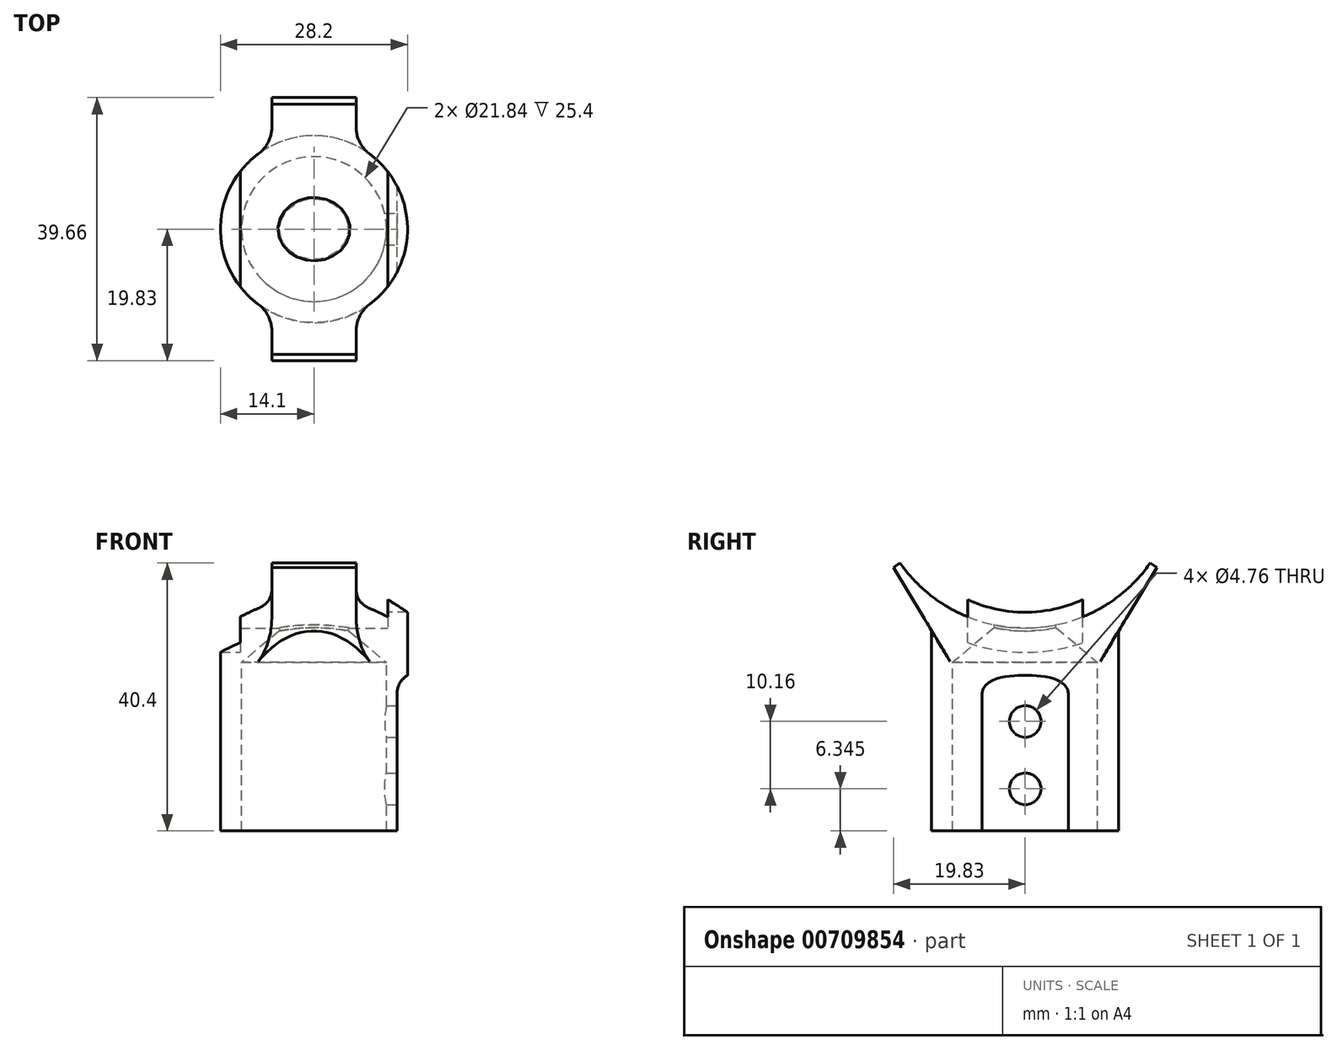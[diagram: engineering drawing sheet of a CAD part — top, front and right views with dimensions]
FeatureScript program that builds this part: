
annotation { "Feature Type Name" : "Feature", "Feature Type Description" : "" }
export const myFeature = defineFeature(function(context is Context, id is Id, definition is map)
    precondition{}
    {
        {
            var Q0;
            Q0=qCreatedBy(makeId("Front.planeOp"),FACE);
            var sketch = newSketch(context, id + "F0", { "sketchPlane" : qUnion([Q0])});
            skLineSegment(sketch, "E0", {"start": v(0, 0) * mm, "end": v(-10.92, -9.16) * mm});
            skLineSegment(sketch, "E1", {"start": v(-10.92, -9.16) * mm, "end": v(-10.92, -34.56) * mm});
            skLineSegment(sketch, "E2", {"start": v(0, 0) * mm, "end": v(0, -71.28) * mm, "construction": true});
            skLineSegment(sketch, "E3", {"start": v(-10.92, -34.56) * mm, "end": v(-14.1, -34.56) * mm});
            skLineSegment(sketch, "E4", {"start": v(-14.1, -34.56) * mm, "end": v(-14.1, 9.52) * mm});
            skLineSegment(sketch, "E5", {"start": v(-14.1, 9.52) * mm, "end": v(0, 9.52) * mm});
            skLineSegment(sketch, "E6", {"start": v(0, 9.52) * mm, "end": v(0, 0) * mm});
            skSolve(sketch);
        }
        {
            var Q0;
            Q0=makeQuery(id+"F0.imprint","IMPRINT",FACE,{"disambiguationData":[TD([[makeQuery(id+"F0.imprint","IMPRINT",EDGE,{"derivedFrom":sQuery(id+"F0.wireOp",EDGE,"E0")}),-1.0]])]});
            var Q1;
            Q1=sQuery(id+"F0.wireOp",EDGE,"E2");
            revolve(context, id + "F1", {"entities" : qUnion([Q0]), "axis" : qUnion([Q1]), "revolveType" : RevolveType.FULL});
        }
        {
            var Q0;
            Q0=makeQuery(id+"F1.opRevolve","SWEPT_EDGE",EDGE,{"disambiguationData":[OSD([sQuery(id+"F0.wireOp",EDGE,"E4"),sQuery(id+"F0.wireOp",EDGE,"E5")])]});
            fillet(context, id + "F2", {"entities" : qUnion([Q0]), "radius" : 2.38 * mm, "tangentPropagation" : true, "allowEdgeOverflow" : false});
        }
        {
            var Q0;
            Q0=qCreatedBy(makeId("Front.planeOp"),FACE);
            var sketch = newSketch(context, id + "F3", { "sketchPlane" : qUnion([Q0])});
            skLineSegment(sketch, "E7", {"start": v(10.92, -10.67) * mm, "end": v(10.92, -36.07) * mm});
            skLineSegment(sketch, "E8", {"start": v(-10.92, -36.07) * mm, "end": v(-10.92, -10.67) * mm});
            skLineSegment(sketch, "E9", {"start": v(-14.1, -36.07) * mm, "end": v(-14.1, 3.17) * mm});
            skLineSegment(sketch, "E10", {"start": v(12.5, -13.84) * mm, "end": v(12.5, -38.6) * mm});
            skLineSegment(sketch, "E11", {"start": v(15.68, -10.67) * mm, "end": v(18.86, -10.67) * mm});
            skLineSegment(sketch, "E12", {"start": v(18.86, -10.67) * mm, "end": v(18.86, -38.6) * mm});
            skLineSegment(sketch, "E13", {"start": v(18.86, -38.6) * mm, "end": v(12.5, -38.6) * mm});
            skPoint(sketch, "E14.visualSharp", {"position": v(12.5, -10.67) * mm});
            skArc(sketch, "E14.filletArc", {"start": v(15.68, -10.67) * mm, "mid": v(13.44, -11.6) * mm, "end": v(12.5, -13.84) * mm});
            skSolve(sketch);
        }
        {
            var Q0;
            Q0=makeQuery(id+"F3.imprint","IMPRINT",FACE,{"disambiguationData":[TD([[makeQuery(id+"F3.imprint","IMPRINT",EDGE,{"derivedFrom":sQuery(id+"F3.wireOp",EDGE,"E10")}),1.0]])]});
            extrude(context, id + "F4", {"entities" : qUnion([Q0]), "operationType" : NewBodyOperationType.REMOVE, "depth" : 25.4 * mm, "hasSecondDirection" : true, "secondDirectionOppositeDirection" : true, "secondDirectionDepth" : 25.4 * mm});
        }
        {
            var Q0;
            Q0=makeQuery(id+"F4.boolean.opBoolean","COPY",FACE,{"derivedFrom":makeQuery(id+"F4.opExtrude","SWEPT_FACE",FACE,{"disambiguationData":[OSD([sQuery(id+"F3.wireOp",EDGE,"E10")])]})});
            var sketch = newSketch(context, id + "F5", { "sketchPlane" : qUnion([Q0])});
            skLineSegment(sketch, "E15", {"start": v(0, -34.56) * mm, "end": v(0, -13.84) * mm, "construction": true});
            skCircle(sketch, "E16", {"center": v(0, -18.05) * mm, "radius": 2.38 * mm});
            skCircle(sketch, "E17", {"center": v(0, -28.21) * mm, "radius": 2.38 * mm});
            skSolve(sketch);
        }
        {
            var Q0;
            Q0=makeQuery(id+"F5.imprint","IMPRINT",FACE,{"disambiguationData":[TD([[makeQuery(id+"F5.imprint","IMPRINT",EDGE,{"derivedFrom":sQuery(id+"F5.wireOp",EDGE,"E16")}),1.0]])]});
            var Q1;
            Q1=makeQuery(id+"F5.imprint","IMPRINT",FACE,{"disambiguationData":[TD([[makeQuery(id+"F5.imprint","IMPRINT",EDGE,{"derivedFrom":sQuery(id+"F5.wireOp",EDGE,"E17")}),1.0]])]});
            extrude(context, id + "F6", {"entities" : qUnion([Q0, Q1]), "operationType" : NewBodyOperationType.REMOVE, "oppositeDirection" : true, "depth" : 6.35 * mm});
        }
        {
            var Q0;
            Q0=qCreatedBy(makeId("Right.planeOp"),FACE);
            var sketch = newSketch(context, id + "F7", { "sketchPlane" : qUnion([Q0])});
            skLineSegment(sketch, "E18", {"start": v(-11.12, -9.33) * mm, "end": v(0, 0) * mm});
            skLineSegment(sketch, "E19", {"start": v(0, 0) * mm, "end": v(11.12, -9.33) * mm});
            skLineSegment(sketch, "E20", {"start": v(-11.12, -9.33) * mm, "end": v(-21.59, 8.08) * mm});
            skLineSegment(sketch, "E21", {"start": v(0, 0) * mm, "end": v(0, 19.05) * mm, "construction": true});
            skLineSegment(sketch, "E22.MirrorCS", {"start": v(11.12, -9.33) * mm, "end": v(21.59, 8.08) * mm});
            skLineSegment(sketch, "E23", {"start": v(-21.6, 8.08) * mm, "end": v(21.59, 8.08) * mm});
            skCircle(sketch, "E24", {"center": v(0, 19.05) * mm, "radius": 23.03 * mm, "construction": true});
            skLineSegment(sketch, "E25", {"start": v(-15.66, 8.08) * mm, "end": v(-19.83, 5.16) * mm});
            skLineSegment(sketch, "E26.MirrorCS", {"start": v(15.66, 8.08) * mm, "end": v(19.83, 5.16) * mm});
            skPoint(sketch, "E27.orphan", {"position": v(-25.04, 1.52) * mm});
            skPoint(sketch, "E28.orphan", {"position": v(25.04, 1.52) * mm});
            skSolve(sketch);
        }
        {
            var Q0;
            Q0=makeQuery(id+"F7.imprint","IMPRINT",FACE,{"disambiguationData":[TD([[makeQuery(id+"F7.imprint","IMPRINT",EDGE,{"derivedFrom":sQuery(id+"F7.wireOp",EDGE,"E18")}),1.0]])]});
            extrude(context, id + "F8", {"entities" : qUnion([Q0]), "operationType" : NewBodyOperationType.ADD, "depth" : 6.35 * mm, "offsetDistance" : 25.4 * mm, "hasSecondDirection" : true, "secondDirectionOppositeDirection" : true, "secondDirectionDepth" : 6.35 * mm});
        }
        {
            var Q0;
            Q0=qCreatedBy(makeId("Right.planeOp"),FACE);
            var sketch = newSketch(context, id + "F9", { "sketchPlane" : qUnion([Q0])});
            skCircle(sketch, "E29.0", {"center": v(0, 19.05) * mm, "radius": 23.03 * mm});
            skSolve(sketch);
        }
        {
            var Q0;
            Q0=makeQuery(id+"F9.imprint","IMPRINT",FACE,{"disambiguationData":[TD([[makeQuery(id+"F9.imprint","IMPRINT",EDGE,{"derivedFrom":sQuery(id+"F9.wireOp",EDGE,"E29.0")}),1.0]])]});
            extrude(context, id + "F10", {"entities" : qUnion([Q0]), "operationType" : NewBodyOperationType.REMOVE, "oppositeDirection" : true, "depth" : 25.4 * mm, "offsetDistance" : 25.4 * mm, "hasSecondDirection" : true, "secondDirectionOppositeDirection" : false, "secondDirectionDepth" : 11.1 * mm});
        }
        {
            var Q0;
            Q0=makeQuery(id+"F8.boolean.opBoolean","INTERSECT",EDGE,{"disambiguationData":[OD(0.0)],"derivedFrom":[makeQuery(id+"F1.opRevolve","SWEPT_FACE",FACE,{"disambiguationData":[OSD([sQuery(id+"F0.wireOp",EDGE,"E4")])]}),makeQuery(id+"F8.opExtrude","CAP_FACE",FACE,{"disambiguationData":[OSD([sQuery(id+"F7.wireOp",EDGE,"E18"),sQuery(id+"F7.wireOp",EDGE,"E19"),sQuery(id+"F7.wireOp",EDGE,"E20"),sQuery(id+"F7.wireOp",EDGE,"E22.MirrorCS"),sQuery(id+"F7.wireOp",EDGE,"E23")])],"isStart":false})]});
            var Q1;
            Q1=makeQuery(id+"F8.boolean.opBoolean","INTERSECT",EDGE,{"disambiguationData":[OD(1.0)],"derivedFrom":[makeQuery(id+"F1.opRevolve","SWEPT_FACE",FACE,{"disambiguationData":[OSD([sQuery(id+"F0.wireOp",EDGE,"E4")])]}),makeQuery(id+"F8.opExtrude","CAP_FACE",FACE,{"disambiguationData":[OSD([sQuery(id+"F7.wireOp",EDGE,"E18"),sQuery(id+"F7.wireOp",EDGE,"E19"),sQuery(id+"F7.wireOp",EDGE,"E20"),sQuery(id+"F7.wireOp",EDGE,"E22.MirrorCS"),sQuery(id+"F7.wireOp",EDGE,"E23")])],"isStart":false})]});
            var Q2;
            Q2=makeQuery(id+"F8.boolean.opBoolean","INTERSECT",EDGE,{"disambiguationData":[OD(1.0)],"derivedFrom":[makeQuery(id+"F1.opRevolve","SWEPT_FACE",FACE,{"disambiguationData":[OSD([sQuery(id+"F0.wireOp",EDGE,"E4")])]}),makeQuery(id+"F8.opExtrude","CAP_FACE",FACE,{"disambiguationData":[OSD([sQuery(id+"F7.wireOp",EDGE,"E18"),sQuery(id+"F7.wireOp",EDGE,"E19"),sQuery(id+"F7.wireOp",EDGE,"E20"),sQuery(id+"F7.wireOp",EDGE,"E22.MirrorCS"),sQuery(id+"F7.wireOp",EDGE,"E23")])],"isStart":true})]});
            var Q3;
            Q3=makeQuery(id+"F8.boolean.opBoolean","INTERSECT",EDGE,{"disambiguationData":[OD(0.0)],"derivedFrom":[makeQuery(id+"F1.opRevolve","SWEPT_FACE",FACE,{"disambiguationData":[OSD([sQuery(id+"F0.wireOp",EDGE,"E4")])]}),makeQuery(id+"F8.opExtrude","CAP_FACE",FACE,{"disambiguationData":[OSD([sQuery(id+"F7.wireOp",EDGE,"E18"),sQuery(id+"F7.wireOp",EDGE,"E19"),sQuery(id+"F7.wireOp",EDGE,"E20"),sQuery(id+"F7.wireOp",EDGE,"E22.MirrorCS"),sQuery(id+"F7.wireOp",EDGE,"E23")])],"isStart":true})]});
            fillet(context, id + "F11", {"entities" : qUnion([Q0, Q1, Q2, Q3]), "radius" : 5.08 * mm, "tangentPropagation" : true, "allowEdgeOverflow" : false});
        }
        {
            var Q0;
            Q0=qCreatedBy(makeId("Right.planeOp"),FACE);
            var sketch = newSketch(context, id + "F12", { "sketchPlane" : qUnion([Q0])});
            skCircle(sketch, "E30", {"center": v(0, 19.05) * mm, "radius": 20.64 * mm});
            skSolve(sketch);
        }
        {
            var Q0;
            Q0=makeQuery(id+"F12.imprint","IMPRINT",FACE,{"disambiguationData":[TD([[makeQuery(id+"F12.imprint","IMPRINT",EDGE,{"derivedFrom":sQuery(id+"F12.wireOp",EDGE,"E30")}),1.0]])]});
            extrude(context, id + "F13", {"entities" : qUnion([Q0]), "operationType" : NewBodyOperationType.REMOVE, "depth" : 25.4 * mm, "offsetDistance" : 25.4 * mm});
        }
        {
            var Q0;
            Q0=qCreatedBy(makeId("Right.planeOp"),FACE);
            cPlane(context, id + "F14", {"entities" : qUnion([Q0]), "cplaneType" : CPlaneType.OFFSET, "offset" : 11.1 * mm, "oppositeDirection" : true, "width" : 152.4 * mm, "height" : 152.4 * mm});
        }
        {
            var Q0;
            Q0=qCreatedBy(id+"F14.planeOp",FACE);
            var sketch = newSketch(context, id + "F15", { "sketchPlane" : qUnion([Q0])});
            skPoint(sketch, "E31.0", {"position": v(0, 19.05) * mm});
            skCircle(sketch, "E32", {"center": v(0, 19.05) * mm, "radius": 26.67 * mm});
            skSolve(sketch);
        }
        {
            var Q0;
            Q0=makeQuery(id+"F15.imprint","IMPRINT",FACE,{"disambiguationData":[TD([[makeQuery(id+"F15.imprint","IMPRINT",EDGE,{"derivedFrom":sQuery(id+"F15.wireOp",EDGE,"E32")}),1.0]])]});
            extrude(context, id + "F16", {"entities" : qUnion([Q0]), "operationType" : NewBodyOperationType.REMOVE, "oppositeDirection" : true, "depth" : 25.4 * mm, "offsetDistance" : 25.4 * mm});
        }
        {
            var Q0;
            Q0=makeQuery(id+"F10.boolean.opBoolean","INTERSECT",EDGE,{"derivedFrom":[makeQuery(id+"F1.opRevolve","SWEPT_FACE",FACE,{"disambiguationData":[OSD([sQuery(id+"F0.wireOp",EDGE,"E0")])]}),makeQuery(id+"F10.opExtrude","SWEPT_FACE",FACE,{"disambiguationData":[OSD([sQuery(id+"F9.wireOp",EDGE,"E29.0")])]})]});
            fillet(context, id + "F17", {"entities" : qUnion([Q0]), "radius" : 0.25 * mm, "tangentPropagation" : true, "allowEdgeOverflow" : false});
        }
        {
            var Q0;
            Q0=makeQuery(id+"F1.opRevolve","SWEPT_BODY",BODY,{"disambiguationData":[OSD([sQuery(id+"F0.wireOp",EDGE,"E0"),sQuery(id+"F0.wireOp",EDGE,"E1"),sQuery(id+"F0.wireOp",EDGE,"E3"),sQuery(id+"F0.wireOp",EDGE,"E4"),sQuery(id+"F0.wireOp",EDGE,"E5"),sQuery(id+"F0.wireOp",EDGE,"E6")])]});
            transform(context, id + "F18", {"entities" : qUnion([Q0]), "transformType" : TransformType.TRANSLATION_3D, "dx" : 0 * mm, "dy" : 0 * mm, "dz" : 0 * mm, "makeCopy" : true});
        }
    });
